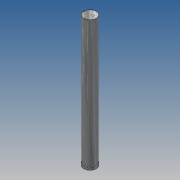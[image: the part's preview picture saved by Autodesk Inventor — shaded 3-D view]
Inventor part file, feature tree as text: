
AUTODESK INVENTOR PART (.ipt)
format: ipt  version: 2015 (Build 190159000, 159)  size: 104,960 bytes
history: native  units: mm
features: sketch x3, extrude x2, revolve x1, projected_geometry x1
ambient origin geometry x8: Origin, YZ Plane, XZ Plane, XY Plane, X Axis, Y Axis, Z Axis, Center Point
bodies: Solid1 (feature_tree)
feature tree (7):
  extrude  "Extrusion1"  Depth=42.0mm TaperAngle=0.0deg
  revolve  "Revolution1"  [1 undecoded]
  extrude  "Extrusion2"  Depth=1.5mm
  sketch  "Sketch1"  dims[d0=4.0mm d1=42.0mm d2=0.0mm]
  sketch  "Sketch2"  dims[d3=0.5mm d4=0.2mm]
  projected_geometry  "Projected Loop1"
  sketch  "Sketch4"  dims[d5=0.8mm d6=1.5mm d7=90.0deg d10=0.2mm d11=0.15mm d12=3.0mm d13=0.0mm]
note: 1 required parameter value undecoded (feature->parameter linkage not recoverable at this tier; creation-order binding heuristic only, values carry confidence <= 0.55)
